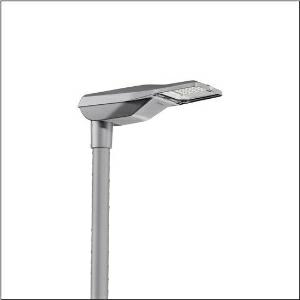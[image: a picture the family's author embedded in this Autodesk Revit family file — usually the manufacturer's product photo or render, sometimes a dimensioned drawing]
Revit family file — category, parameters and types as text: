
# Revit family: streetlight_sl_21_iq_micro___stw1_0a_5xe1e31g08cb_d673
name_source: partatom
category: Lighting Fixtures
units: mm (PartAtom-declared; Revit-internal decimal feet)

## family parameters
Cut with Voids When Loaded = No
Host = Face
Light Source = No
Part Type = Normal
Room Calculation Point = No
Round Connector Dimension = Use Diameter
Shared = No

## types (1)
- --- (1 x LED, 2870 lm, 19.4 W, 3000K)
    Apparent Load = 19 VA
    CIE Flux Codes = 38 75 98 100 100
    Color Rendering = 70
    Color Temperature = 3000K
    Default Elevation = 1800 mm
    Description = Streetlight SL 21 iQ micro, mast luminaire, primary light control with lens, of PMMA, primary optical cover: cover, of toughened safety glass, transparent, light distribution: STW1.0a, light emission: direct distribution, primary light characteristic: asymmetric, installation type: post-top, side-entry, LED, High Power LED, rated luminous flux: 2.870lm, luminous efficacy: 148lm/W, light colour: 730, colour temperature: 3000K, control gear: iQ Street-Remote, control: Street-Remote, Auto-Match, Temp-Guard, Lumen-Switch, Night-Set, Smart-Wire, Light-Fading, Desk-Remote (wireless, voltage-free reading and setting of iQ features in the workshop via application-optimized NFC function/RFID function), optimised constant luminous flux control (CLO 2.0), pre-setting: linear dimming characteristic, mains connection: 220..240V, AC, 50/60Hz, start of lifetime: 19W, end of service life: 20W, reduction: 10W, luminaire housing, of diecast aluminium, powder-coated, SITECO metallic grey (DB 702S), corrosivity category C5 high according to DIN EN ISO 12944, please order mast flange separately, inclination adjustable: 0°, 5°, 10°, 15°, sealing non-destructively replaceable, multi-level sealing system, length: 528mm, width: 235mm, height: 110mm, mast flange for spigot size: 42mm (side-entry): 5XC10008XM4, 60/48mm (side-entry/post-top): 5XC10108XM2, 76/60mm (side-entry/post-top): 5XC10108XM1, protection rating (complete): IP66, insulation class (complete): insulation class II (safety insulation), certification: CE, ENEC, ENEC+, VDE, impact resistance: IK10, permissible operating ambient temperature for outdoor applications: -40..+50°C, standard-compliant lighting for roads and squares, packaging unit: 1 piece

Light Distribution: STW1.0a
    Height = 110 mm
    Lamp = 1 x LED
    Lamp Light Flux = 2870 lm
    Lamp Power = 19.4 W
    Lamp count = 1
    Length = 528 mm
    Luminous efficacy = 148 lm/W
    Manufacturer = Siteco
    ModVariant = No
    Model = 5XE1E31G08CB
    Number of Poles = 1
    OnlyDefault = Yes
    Power Factor = 1
    Product Name = Streetlight SL 21 iQ micro | STW1.0a
    Product group = mast luminaire | pylon top
    ProductGroupID = 6100
    Protection Class = Protection class II
    Protection Degree = IP 66
    RLX_Detail_Level = 1
    RLX_Emergency_Light_Flux = 0 lm
    RLX_Emergency_Type = 0
    RLX_Emergency_Type_DB = No
    RlxData = <blob elided: 98925 chars, md5=fc87ff48>
    Socket = socket
    Standby Power = 0 W
    System Light Flux = 2870 lm
    System Power = 19 W
    Type Comments = factory setting: luminous flux: 100 % | dim-lin: 254 | 387 mA
    Type Image = l_1006881.jpg
    URL = http://relux.com
    VarID = @adj_138355
    Voltage = 0 V
    Weight = 0.00 kg
    Width = 235 mm

## geometry (parser evidence)
native form markers: Blend x4, Sweep x12
no freeform markers — native parametric forms only
